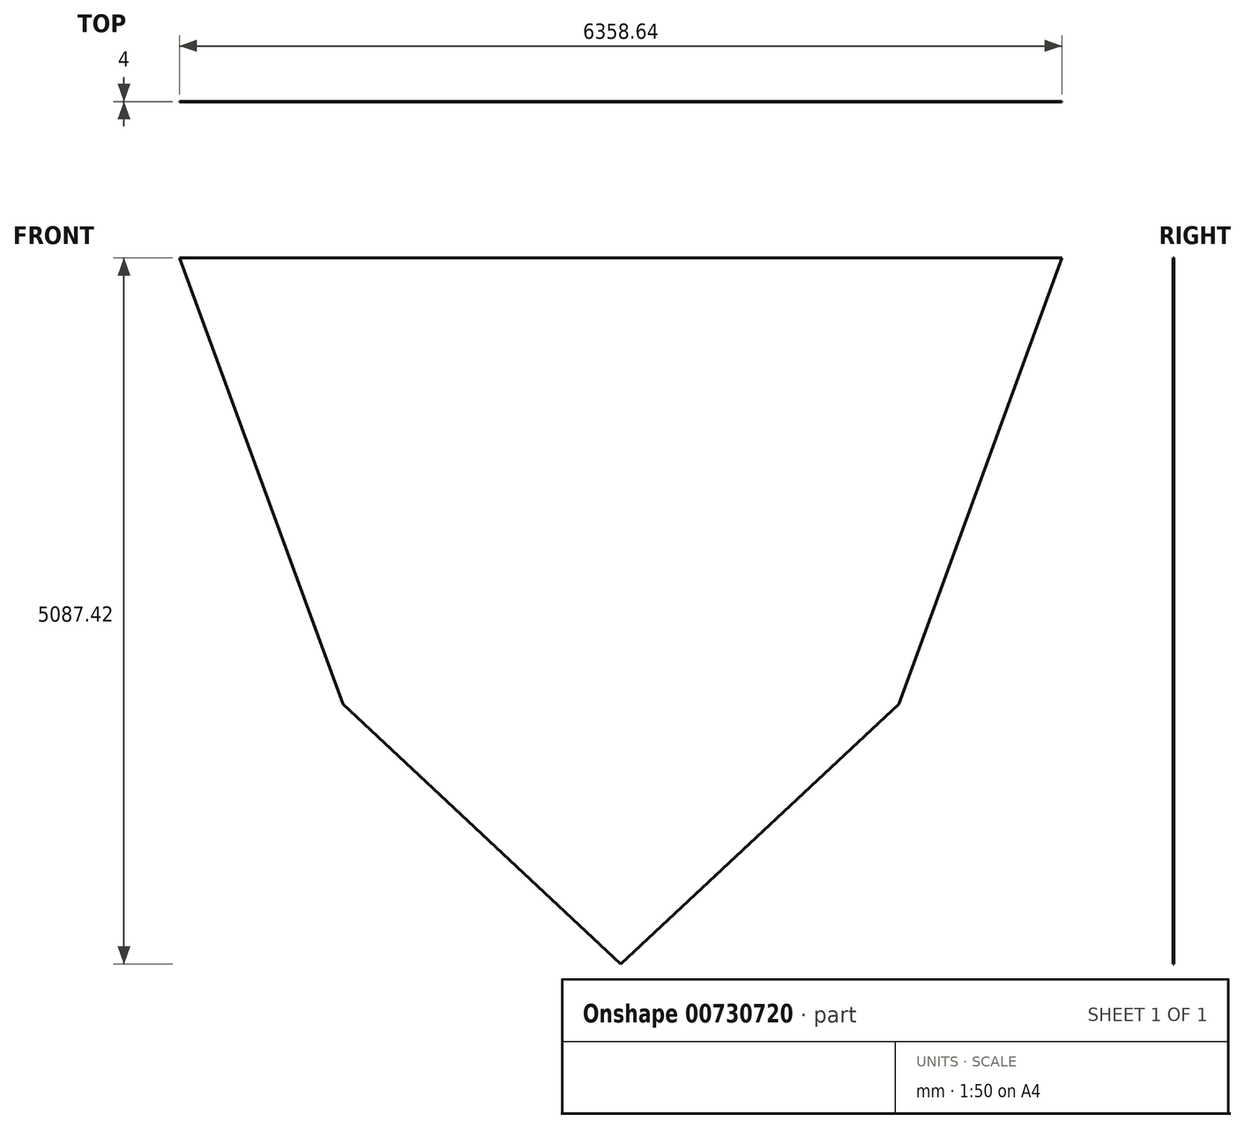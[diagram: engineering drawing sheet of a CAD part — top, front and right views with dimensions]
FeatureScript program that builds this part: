
annotation { "Feature Type Name" : "Feature", "Feature Type Description" : "" }
export const myFeature = defineFeature(function(context is Context, id is Id, definition is map)
    precondition{}
    {
        {
            var Q0;
            Q0=qCreatedBy(makeId("Front.planeOp"),FACE);
            var sketch = newSketch(context, id + "F0", { "sketchPlane" : qUnion([Q0])});
            skLineSegment(sketch, "E0", {"start": v(-3179.32, 2543.7) * mm, "end": v(0, 2543.7) * mm});
            skLineSegment(sketch, "E1", {"start": v(0, 2543.7) * mm, "end": v(0, 2416.7) * mm});
            skLineSegment(sketch, "E2", {"start": v(0, 2416.7) * mm, "end": v(0, 2543.7) * mm});
            skLineSegment(sketch, "E3", {"start": v(0, 2543.7) * mm, "end": v(3179.32, 2543.7) * mm});
            skLineSegment(sketch, "E4", {"start": v(3179.32, 2543.7) * mm, "end": v(2002.03, -672.46) * mm});
            skLineSegment(sketch, "E5", {"start": v(2002.03, -672.46) * mm, "end": v(0, -2543.7) * mm});
            skLineSegment(sketch, "E6", {"start": v(0, -2543.7) * mm, "end": v(-2002.03, -672.46) * mm});
            skLineSegment(sketch, "E7", {"start": v(-2002.03, -672.46) * mm, "end": v(-3179.32, 2543.7) * mm});
            skSolve(sketch);
        }
        {
            var Q0;
            Q0 = qSketchRegion(id + "F0", true);
            extrude(context, id + "F1", {"entities" : qUnion([Q0]), "depth" : 4 * mm, "offsetDistance" : 25 * mm});
        }
    });
